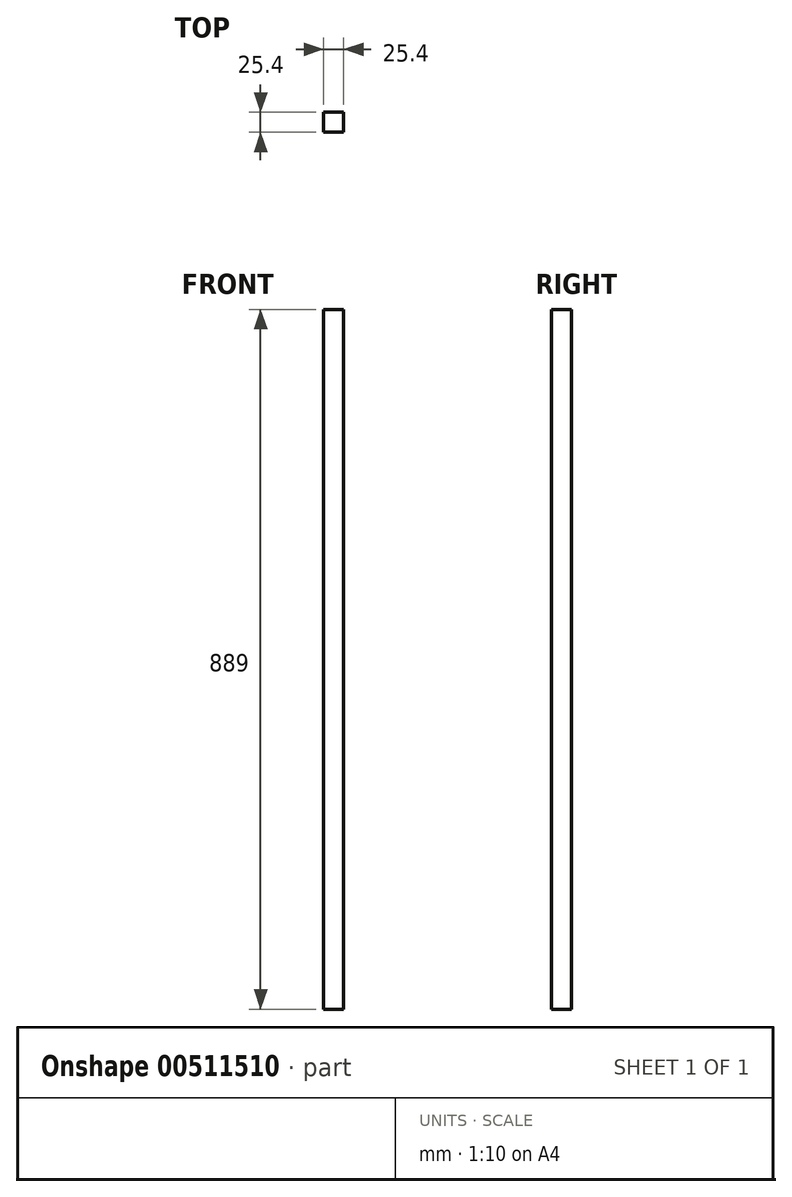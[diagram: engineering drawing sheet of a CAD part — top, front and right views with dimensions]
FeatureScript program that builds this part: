
annotation { "Feature Type Name" : "Feature", "Feature Type Description" : "" }
export const myFeature = defineFeature(function(context is Context, id is Id, definition is map)
    precondition{}
    {
        {
            var Q0;
            Q0=qCreatedBy(makeId("Top.planeOp"),FACE);
            var sketch = newSketch(context, id + "F0", { "sketchPlane" : qUnion([Q0])});
            skLineSegment(sketch, "E0.bottom", {"start": v(12.7, 12.7) * mm, "end": v(-12.7, 12.7) * mm});
            skLineSegment(sketch, "E0.top", {"start": v(12.7, -12.7) * mm, "end": v(-12.7, -12.7) * mm});
            skLineSegment(sketch, "E0.left", {"start": v(12.7, 12.7) * mm, "end": v(12.7, -12.7) * mm});
            skLineSegment(sketch, "E0.right", {"start": v(-12.7, 12.7) * mm, "end": v(-12.7, -12.7) * mm});
            skPoint(sketch, "E0.middle", {"position": v(0, 0) * mm});
            skSolve(sketch);
        }
        {
            var Q0;
            Q0=makeQuery(id+"F0.imprint","IMPRINT",FACE,{"disambiguationData":[TD([[makeQuery(id+"F0.imprint","IMPRINT",EDGE,{"derivedFrom":sQuery(id+"F0.wireOp",EDGE,"E0.bottom")}),1.0]])]});
            extrude(context, id + "F1", {"entities" : qUnion([Q0]), "depth" : 889 * mm, "offsetDistance" : 25.4 * mm});
        }
    });
